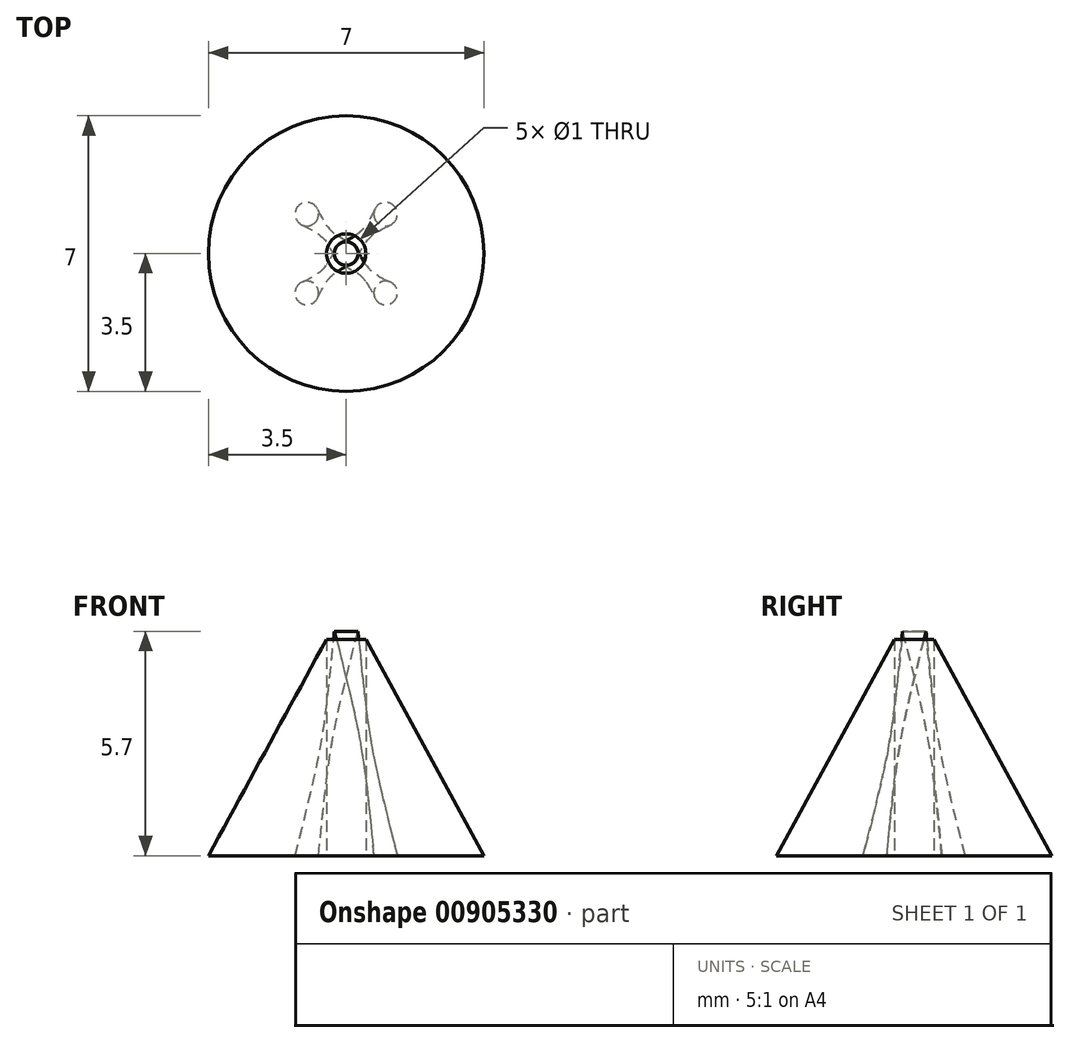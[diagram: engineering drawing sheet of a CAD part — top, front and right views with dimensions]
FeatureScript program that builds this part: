
annotation { "Feature Type Name" : "Feature", "Feature Type Description" : "" }
export const myFeature = defineFeature(function(context is Context, id is Id, definition is map)
    precondition{}
    {
        {
            var Q0;
            Q0=qCreatedBy(makeId("Front.planeOp"),FACE);
            var sketch = newSketch(context, id + "F0", { "sketchPlane" : qUnion([Q0])});
            skLineSegment(sketch, "E0", {"start": v(-0.5, 0) * mm, "end": v(-0.5, 5.5) * mm});
            skLineSegment(sketch, "E1", {"start": v(-0.5, 5.5) * mm, "end": v(-3.5, 0) * mm});
            skLineSegment(sketch, "E2", {"start": v(-3.5, 0) * mm, "end": v(-0.5, 0) * mm});
            skLineSegment(sketch, "E3", {"start": v(-0.5, 0) * mm, "end": v(0, 0) * mm});
            skLineSegment(sketch, "E4", {"start": v(0, 0) * mm, "end": v(0, 5.5) * mm});
            skLineSegment(sketch, "E5", {"start": v(0, 5.5) * mm, "end": v(-0.5, 5.5) * mm});
            skSolve(sketch);
        }
        {
            var Q0;
            Q0=makeQuery(id+"F0.imprint","IMPRINT",FACE,{"disambiguationData":[TD([[makeQuery(id+"F0.imprint","IMPRINT",EDGE,{"derivedFrom":sQuery(id+"F0.wireOp",EDGE,"E0")}),1.0]])]});
            var Q1;
            Q1=sQuery(id+"F0.wireOp",EDGE,"E4");
            revolve(context, id + "F1", {"surfaceOperationType" : NewSurfaceOperationType.NEW, "entities" : qUnion([Q0]), "axis" : qUnion([Q1]), "revolveType" : RevolveType.FULL});
        }
        {
            var Q0;
            Q0=makeQuery(id+"F1.opRevolve","SWEPT_FACE",FACE,{"disambiguationData":[OSD([sQuery(id+"F0.wireOp",EDGE,"E2")])]});
            var sketch = newSketch(context, id + "F2", { "sketchPlane" : qUnion([Q0])});
            skPoint(sketch, "E6.middle", {"position": v(0, 0) * mm});
            skCircle(sketch, "E7", {"center": v(-1, 1) * mm, "radius": 0.3 * mm});
            skCircle(sketch, "E8", {"center": v(1, 1) * mm, "radius": 0.3 * mm});
            skCircle(sketch, "E9", {"center": v(-1, -1) * mm, "radius": 0.3 * mm});
            skCircle(sketch, "E10", {"center": v(1, -1) * mm, "radius": 0.3 * mm});
            skSolve(sketch);
        }
        {
            var Q0;
            Q0=makeQuery(id+"F2.imprint","IMPRINT",FACE,{"disambiguationData":[TD([[makeQuery(id+"F2.imprint","IMPRINT",EDGE,{"derivedFrom":makeQuery(id+"F1.opRevolve","SWEPT_EDGE",EDGE,{"disambiguationData":[OSD([sQuery(id+"F0.wireOp",EDGE,"E0"),sQuery(id+"F0.wireOp",EDGE,"E2"),sQuery(id+"F0.wireOp",EDGE,"E3")])]})}),1.0]])]});
            cPlane(context, id + "F3", {"entities" : qUnion([Q0]), "cplaneType" : CPlaneType.OFFSET, "offset" : 5.7 * mm, "oppositeDirection" : true, "width" : 150 * mm, "height" : 150 * mm});
        }
        {
            var Q0;
            Q0=qCreatedBy(id+"F3.planeOp",FACE);
            var sketch = newSketch(context, id + "F4", { "sketchPlane" : qUnion([Q0])});
            skCircle(sketch, "E11", {"center": v(0, 0) * mm, "radius": 0.3 * mm});
            skSolve(sketch);
        }
        {
            var Q1;
            Q1=makeQuery(id+"F4.imprint","IMPRINT",FACE,{"disambiguationData":[TD([[makeQuery(id+"F4.imprint","IMPRINT",EDGE,{"derivedFrom":sQuery(id+"F4.wireOp",EDGE,"E11")}),1.0]])]});
            var Q2;
            Q2=makeQuery(id+"F2.imprint","IMPRINT",FACE,{"disambiguationData":[TD([[makeQuery(id+"F2.imprint","IMPRINT",EDGE,{"derivedFrom":sQuery(id+"F2.wireOp",EDGE,"E9")}),1.0]])]});
            loft(context, id + "F5", {"sheetProfilesArray" : [{ "sheetProfileEntities" : qUnion([Q1]) }, { "sheetProfileEntities" : qUnion([Q2]) }]});
        }
        {
            var Q0;
            Q0=makeQuery(id+"F5.opLoft","CAP_FACE",FACE,{"disambiguationData":[OSD([makeQuery(id+"F4.imprint","IMPRINT",FACE,{"disambiguationData":[TD([[makeQuery(id+"F4.imprint","IMPRINT",EDGE,{"derivedFrom":sQuery(id+"F4.wireOp",EDGE,"E11")}),1.0]])]})])],"isStart":true});
            var Q1;
            Q1=makeQuery(id+"F2.imprint","IMPRINT",FACE,{"disambiguationData":[TD([[makeQuery(id+"F2.imprint","IMPRINT",EDGE,{"derivedFrom":sQuery(id+"F2.wireOp",EDGE,"E7")}),1.0]])]});
            loft(context, id + "F6", {"sheetProfilesArray" : [{ "sheetProfileEntities" : qUnion([Q0]) }, { "sheetProfileEntities" : qUnion([Q1]) }]});
        }
        {
            var Q0;
            Q0=makeQuery(id+"F2.imprint","IMPRINT",FACE,{"disambiguationData":[TD([[makeQuery(id+"F2.imprint","IMPRINT",EDGE,{"derivedFrom":sQuery(id+"F2.wireOp",EDGE,"E8")}),1.0]])]});
            var Q1;
            Q1=makeQuery(id+"F5.opLoft","CAP_FACE",FACE,{"disambiguationData":[OSD([makeQuery(id+"F4.imprint","IMPRINT",FACE,{"disambiguationData":[TD([[makeQuery(id+"F4.imprint","IMPRINT",EDGE,{"derivedFrom":sQuery(id+"F4.wireOp",EDGE,"E11")}),1.0]])]})])],"isStart":true});
            loft(context, id + "F7", {"sheetProfilesArray" : [{ "sheetProfileEntities" : qUnion([Q0]) }, { "sheetProfileEntities" : qUnion([Q1]) }]});
        }
        {
            var Q0;
            Q0=makeQuery(id+"F2.imprint","IMPRINT",FACE,{"disambiguationData":[TD([[makeQuery(id+"F2.imprint","IMPRINT",EDGE,{"derivedFrom":sQuery(id+"F2.wireOp",EDGE,"E10")}),1.0]])]});
            var Q1;
            Q1=makeQuery(id+"F6.opLoft","CAP_FACE",FACE,{"disambiguationData":[OSD([makeQuery(id+"F4.imprint","IMPRINT",FACE,{"disambiguationData":[TD([[makeQuery(id+"F4.imprint","IMPRINT",EDGE,{"derivedFrom":sQuery(id+"F4.wireOp",EDGE,"E11")}),1.0]])]})])],"isStart":true});
            loft(context, id + "F8", {"sheetProfilesArray" : [{ "sheetProfileEntities" : qUnion([Q0]) }, { "sheetProfileEntities" : qUnion([Q1]) }]});
        }
    });
